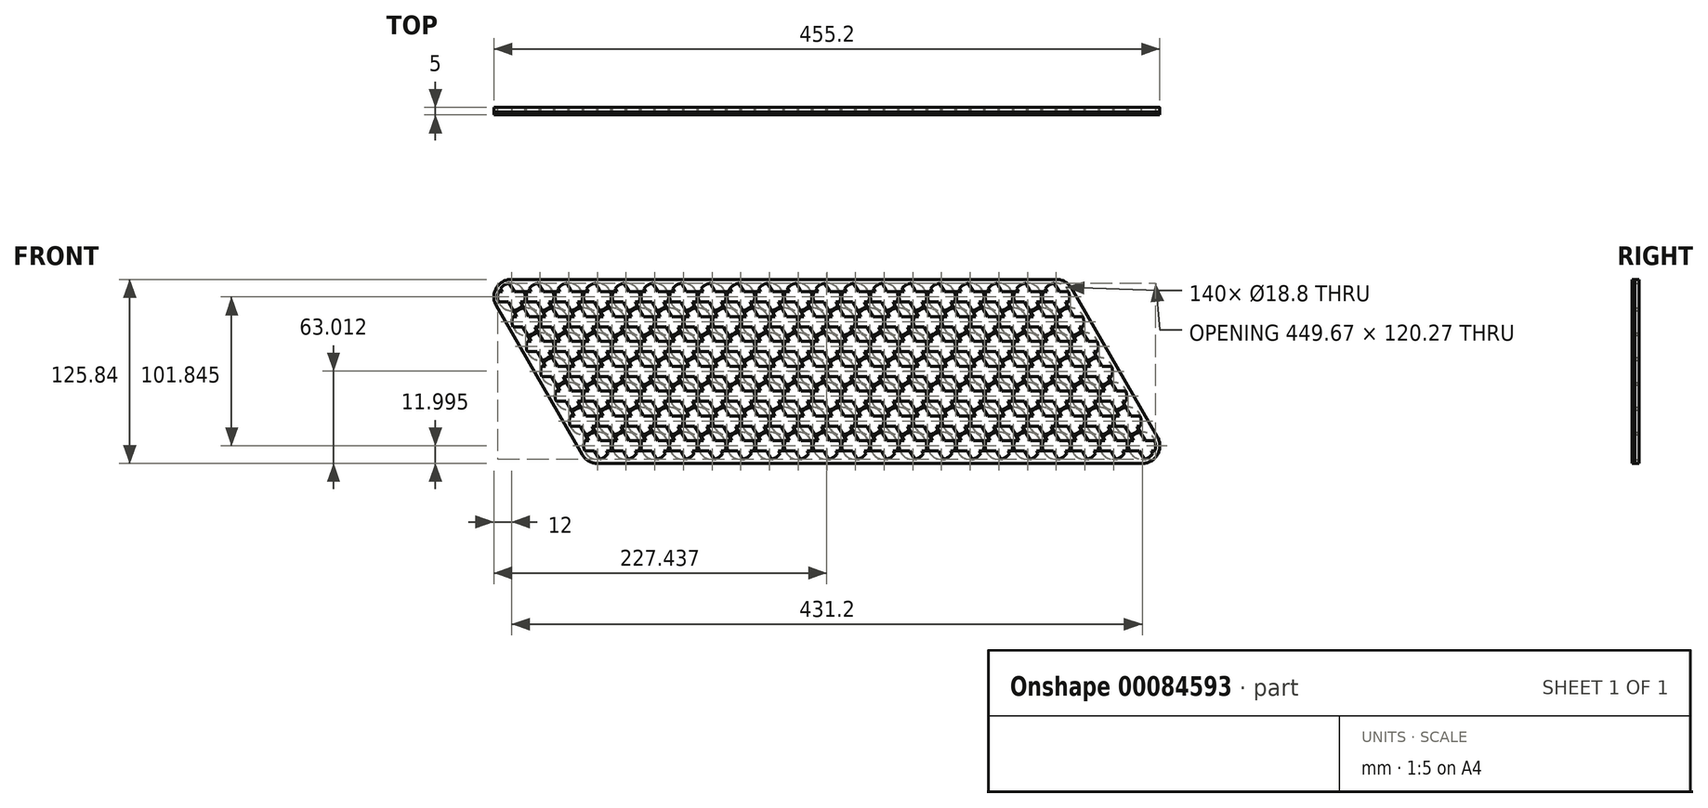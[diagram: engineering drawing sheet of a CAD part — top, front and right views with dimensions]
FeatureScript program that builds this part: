
annotation { "Feature Type Name" : "Feature", "Feature Type Description" : "" }
export const myFeature = defineFeature(function(context is Context, id is Id, definition is map)
    precondition{}
    {
        {
            var Q0;
            Q0=qCreatedBy(makeId("Front.planeOp"),FACE);
            var sketch = newSketch(context, id + "F0", { "sketchPlane" : qUnion([Q0]) });
            skLineSegment(sketch, "E0", {"start": v(0, 0) * mm, "end": v(79.44, 0) * mm, "construction": true});
            skLineSegment(sketch, "E1", {"start": v(0, 0) * mm, "end": v(43.4, -75.16) * mm, "construction": true});
            skCircle(sketch, "E2", {"center": v(0, 0) * mm, "radius": 9.4 * mm});
            skCircle(sketch, "E3.1.0.0", {"center": v(19.6, 0) * mm, "radius": 9.4 * mm});
            skCircle(sketch, "E3.2.0.0", {"center": v(39.2, 0) * mm, "radius": 9.4 * mm});
            skCircle(sketch, "E3.3.0.0", {"center": v(58.8, 0) * mm, "radius": 9.4 * mm});
            skCircle(sketch, "E3.4.0.0", {"center": v(78.4, 0) * mm, "radius": 9.4 * mm});
            skCircle(sketch, "E3.5.0.0", {"center": v(98, 0) * mm, "radius": 9.4 * mm});
            skCircle(sketch, "E3.6.0.0", {"center": v(117.6, 0) * mm, "radius": 9.4 * mm});
            skCircle(sketch, "E3.7.0.0", {"center": v(137.2, 0) * mm, "radius": 9.4 * mm});
            skCircle(sketch, "E3.8.0.0", {"center": v(156.8, 0) * mm, "radius": 9.4 * mm});
            skCircle(sketch, "E3.9.0.0", {"center": v(176.4, 0) * mm, "radius": 9.4 * mm});
            skCircle(sketch, "E3.10.0.0", {"center": v(196, 0) * mm, "radius": 9.4 * mm});
            skCircle(sketch, "E3.11.0.0", {"center": v(215.6, 0) * mm, "radius": 9.4 * mm});
            skCircle(sketch, "E3.12.0.0", {"center": v(235.2, 0) * mm, "radius": 9.4 * mm});
            skCircle(sketch, "E3.13.0.0", {"center": v(254.8, 0) * mm, "radius": 9.4 * mm});
            skCircle(sketch, "E3.14.0.0", {"center": v(274.4, 0) * mm, "radius": 9.4 * mm});
            skCircle(sketch, "E3.15.0.0", {"center": v(294, 0) * mm, "radius": 9.4 * mm});
            skCircle(sketch, "E3.16.0.0", {"center": v(313.6, 0) * mm, "radius": 9.4 * mm});
            skCircle(sketch, "E3.17.0.0", {"center": v(333.2, 0) * mm, "radius": 9.4 * mm});
            skCircle(sketch, "E3.18.0.0", {"center": v(352.8, 0) * mm, "radius": 9.4 * mm});
            skCircle(sketch, "E3.19.0.0", {"center": v(372.4, 0) * mm, "radius": 9.4 * mm});
            skLineSegment(sketch, "E3.direction1", {"start": v(0, 0) * mm, "end": v(19.6, 0) * mm, "construction": true});
            skCircle(sketch, "E4.1.0.0", {"center": v(9.8, -16.97) * mm, "radius": 9.4 * mm});
            skCircle(sketch, "E4.2.0.0", {"center": v(19.6, -33.95) * mm, "radius": 9.4 * mm});
            skCircle(sketch, "E4.3.0.0", {"center": v(29.4, -50.92) * mm, "radius": 9.4 * mm});
            skCircle(sketch, "E4.4.0.0", {"center": v(39.2, -67.9) * mm, "radius": 9.4 * mm});
            skCircle(sketch, "E4.5.0.0", {"center": v(49, -84.87) * mm, "radius": 9.4 * mm});
            skCircle(sketch, "E4.6.0.0", {"center": v(58.8, -101.84) * mm, "radius": 9.4 * mm});
            skLineSegment(sketch, "E4.direction1", {"start": v(0, 0) * mm, "end": v(9.8, -16.97) * mm, "construction": true});
            skCircle(sketch, "E5.1.0.0", {"center": v(29.4, -16.97) * mm, "radius": 9.4 * mm});
            skCircle(sketch, "E5.1.0.1", {"center": v(39.2, -33.95) * mm, "radius": 9.4 * mm});
            skCircle(sketch, "E5.1.0.2", {"center": v(49, -50.92) * mm, "radius": 9.4 * mm});
            skCircle(sketch, "E5.1.0.3", {"center": v(58.8, -67.9) * mm, "radius": 9.4 * mm});
            skCircle(sketch, "E5.1.0.4", {"center": v(68.6, -84.87) * mm, "radius": 9.4 * mm});
            skCircle(sketch, "E5.1.0.5", {"center": v(78.4, -101.84) * mm, "radius": 9.4 * mm});
            skCircle(sketch, "E5.2.0.0", {"center": v(49, -16.97) * mm, "radius": 9.4 * mm});
            skCircle(sketch, "E5.2.0.1", {"center": v(58.8, -33.95) * mm, "radius": 9.4 * mm});
            skCircle(sketch, "E5.2.0.2", {"center": v(68.6, -50.92) * mm, "radius": 9.4 * mm});
            skCircle(sketch, "E5.2.0.3", {"center": v(78.4, -67.9) * mm, "radius": 9.4 * mm});
            skCircle(sketch, "E5.2.0.4", {"center": v(88.2, -84.87) * mm, "radius": 9.4 * mm});
            skCircle(sketch, "E5.2.0.5", {"center": v(98, -101.84) * mm, "radius": 9.4 * mm});
            skCircle(sketch, "E5.3.0.0", {"center": v(68.6, -16.97) * mm, "radius": 9.4 * mm});
            skCircle(sketch, "E5.3.0.1", {"center": v(78.4, -33.95) * mm, "radius": 9.4 * mm});
            skCircle(sketch, "E5.3.0.2", {"center": v(88.2, -50.92) * mm, "radius": 9.4 * mm});
            skCircle(sketch, "E5.3.0.3", {"center": v(98, -67.9) * mm, "radius": 9.4 * mm});
            skCircle(sketch, "E5.3.0.4", {"center": v(107.8, -84.87) * mm, "radius": 9.4 * mm});
            skCircle(sketch, "E5.3.0.5", {"center": v(117.6, -101.84) * mm, "radius": 9.4 * mm});
            skCircle(sketch, "E5.4.0.0", {"center": v(88.2, -16.97) * mm, "radius": 9.4 * mm});
            skCircle(sketch, "E5.4.0.1", {"center": v(98, -33.95) * mm, "radius": 9.4 * mm});
            skCircle(sketch, "E5.4.0.2", {"center": v(107.8, -50.92) * mm, "radius": 9.4 * mm});
            skCircle(sketch, "E5.4.0.3", {"center": v(117.6, -67.9) * mm, "radius": 9.4 * mm});
            skCircle(sketch, "E5.4.0.4", {"center": v(127.4, -84.87) * mm, "radius": 9.4 * mm});
            skCircle(sketch, "E5.4.0.5", {"center": v(137.2, -101.84) * mm, "radius": 9.4 * mm});
            skCircle(sketch, "E5.5.0.0", {"center": v(107.8, -16.97) * mm, "radius": 9.4 * mm});
            skCircle(sketch, "E5.5.0.1", {"center": v(117.6, -33.95) * mm, "radius": 9.4 * mm});
            skCircle(sketch, "E5.5.0.2", {"center": v(127.4, -50.92) * mm, "radius": 9.4 * mm});
            skCircle(sketch, "E5.5.0.3", {"center": v(137.2, -67.9) * mm, "radius": 9.4 * mm});
            skCircle(sketch, "E5.5.0.4", {"center": v(147, -84.87) * mm, "radius": 9.4 * mm});
            skCircle(sketch, "E5.5.0.5", {"center": v(156.8, -101.84) * mm, "radius": 9.4 * mm});
            skCircle(sketch, "E5.6.0.0", {"center": v(127.4, -16.97) * mm, "radius": 9.4 * mm});
            skCircle(sketch, "E5.6.0.1", {"center": v(137.2, -33.95) * mm, "radius": 9.4 * mm});
            skCircle(sketch, "E5.6.0.2", {"center": v(147, -50.92) * mm, "radius": 9.4 * mm});
            skCircle(sketch, "E5.6.0.3", {"center": v(156.8, -67.9) * mm, "radius": 9.4 * mm});
            skCircle(sketch, "E5.6.0.4", {"center": v(166.6, -84.87) * mm, "radius": 9.4 * mm});
            skCircle(sketch, "E5.6.0.5", {"center": v(176.4, -101.84) * mm, "radius": 9.4 * mm});
            skCircle(sketch, "E5.7.0.0", {"center": v(147, -16.97) * mm, "radius": 9.4 * mm});
            skCircle(sketch, "E5.7.0.1", {"center": v(156.8, -33.95) * mm, "radius": 9.4 * mm});
            skCircle(sketch, "E5.7.0.2", {"center": v(166.6, -50.92) * mm, "radius": 9.4 * mm});
            skCircle(sketch, "E5.7.0.3", {"center": v(176.4, -67.9) * mm, "radius": 9.4 * mm});
            skCircle(sketch, "E5.7.0.4", {"center": v(186.2, -84.87) * mm, "radius": 9.4 * mm});
            skCircle(sketch, "E5.7.0.5", {"center": v(196, -101.84) * mm, "radius": 9.4 * mm});
            skCircle(sketch, "E5.8.0.0", {"center": v(166.6, -16.97) * mm, "radius": 9.4 * mm});
            skCircle(sketch, "E5.8.0.1", {"center": v(176.4, -33.95) * mm, "radius": 9.4 * mm});
            skCircle(sketch, "E5.8.0.2", {"center": v(186.2, -50.92) * mm, "radius": 9.4 * mm});
            skCircle(sketch, "E5.8.0.3", {"center": v(196, -67.9) * mm, "radius": 9.4 * mm});
            skCircle(sketch, "E5.8.0.4", {"center": v(205.8, -84.87) * mm, "radius": 9.4 * mm});
            skCircle(sketch, "E5.8.0.5", {"center": v(215.6, -101.84) * mm, "radius": 9.4 * mm});
            skCircle(sketch, "E5.9.0.0", {"center": v(186.2, -16.97) * mm, "radius": 9.4 * mm});
            skCircle(sketch, "E5.9.0.1", {"center": v(196, -33.95) * mm, "radius": 9.4 * mm});
            skCircle(sketch, "E5.9.0.2", {"center": v(205.8, -50.92) * mm, "radius": 9.4 * mm});
            skCircle(sketch, "E5.9.0.3", {"center": v(215.6, -67.9) * mm, "radius": 9.4 * mm});
            skCircle(sketch, "E5.9.0.4", {"center": v(225.4, -84.87) * mm, "radius": 9.4 * mm});
            skCircle(sketch, "E5.9.0.5", {"center": v(235.2, -101.84) * mm, "radius": 9.4 * mm});
            skCircle(sketch, "E5.10.0.0", {"center": v(205.8, -16.97) * mm, "radius": 9.4 * mm});
            skCircle(sketch, "E5.10.0.1", {"center": v(215.6, -33.95) * mm, "radius": 9.4 * mm});
            skCircle(sketch, "E5.10.0.2", {"center": v(225.4, -50.92) * mm, "radius": 9.4 * mm});
            skCircle(sketch, "E5.10.0.3", {"center": v(235.2, -67.9) * mm, "radius": 9.4 * mm});
            skCircle(sketch, "E5.10.0.4", {"center": v(245, -84.87) * mm, "radius": 9.4 * mm});
            skCircle(sketch, "E5.10.0.5", {"center": v(254.8, -101.84) * mm, "radius": 9.4 * mm});
            skCircle(sketch, "E5.11.0.0", {"center": v(225.4, -16.97) * mm, "radius": 9.4 * mm});
            skCircle(sketch, "E5.11.0.1", {"center": v(235.2, -33.95) * mm, "radius": 9.4 * mm});
            skCircle(sketch, "E5.11.0.2", {"center": v(245, -50.92) * mm, "radius": 9.4 * mm});
            skCircle(sketch, "E5.11.0.3", {"center": v(254.8, -67.9) * mm, "radius": 9.4 * mm});
            skCircle(sketch, "E5.11.0.4", {"center": v(264.6, -84.87) * mm, "radius": 9.4 * mm});
            skCircle(sketch, "E5.11.0.5", {"center": v(274.4, -101.84) * mm, "radius": 9.4 * mm});
            skCircle(sketch, "E5.12.0.0", {"center": v(245, -16.97) * mm, "radius": 9.4 * mm});
            skCircle(sketch, "E5.12.0.1", {"center": v(254.8, -33.95) * mm, "radius": 9.4 * mm});
            skCircle(sketch, "E5.12.0.2", {"center": v(264.6, -50.92) * mm, "radius": 9.4 * mm});
            skCircle(sketch, "E5.12.0.3", {"center": v(274.4, -67.9) * mm, "radius": 9.4 * mm});
            skCircle(sketch, "E5.12.0.4", {"center": v(284.2, -84.87) * mm, "radius": 9.4 * mm});
            skCircle(sketch, "E5.12.0.5", {"center": v(294, -101.84) * mm, "radius": 9.4 * mm});
            skCircle(sketch, "E5.13.0.0", {"center": v(264.6, -16.97) * mm, "radius": 9.4 * mm});
            skCircle(sketch, "E5.13.0.1", {"center": v(274.4, -33.95) * mm, "radius": 9.4 * mm});
            skCircle(sketch, "E5.13.0.2", {"center": v(284.2, -50.92) * mm, "radius": 9.4 * mm});
            skCircle(sketch, "E5.13.0.3", {"center": v(294, -67.9) * mm, "radius": 9.4 * mm});
            skCircle(sketch, "E5.13.0.4", {"center": v(303.8, -84.87) * mm, "radius": 9.4 * mm});
            skCircle(sketch, "E5.13.0.5", {"center": v(313.6, -101.84) * mm, "radius": 9.4 * mm});
            skCircle(sketch, "E5.14.0.0", {"center": v(284.2, -16.97) * mm, "radius": 9.4 * mm});
            skCircle(sketch, "E5.14.0.1", {"center": v(294, -33.95) * mm, "radius": 9.4 * mm});
            skCircle(sketch, "E5.14.0.2", {"center": v(303.8, -50.92) * mm, "radius": 9.4 * mm});
            skCircle(sketch, "E5.14.0.3", {"center": v(313.6, -67.9) * mm, "radius": 9.4 * mm});
            skCircle(sketch, "E5.14.0.4", {"center": v(323.4, -84.87) * mm, "radius": 9.4 * mm});
            skCircle(sketch, "E5.14.0.5", {"center": v(333.2, -101.84) * mm, "radius": 9.4 * mm});
            skCircle(sketch, "E5.15.0.0", {"center": v(303.8, -16.97) * mm, "radius": 9.4 * mm});
            skCircle(sketch, "E5.15.0.1", {"center": v(313.6, -33.95) * mm, "radius": 9.4 * mm});
            skCircle(sketch, "E5.15.0.2", {"center": v(323.4, -50.92) * mm, "radius": 9.4 * mm});
            skCircle(sketch, "E5.15.0.3", {"center": v(333.2, -67.9) * mm, "radius": 9.4 * mm});
            skCircle(sketch, "E5.15.0.4", {"center": v(343, -84.87) * mm, "radius": 9.4 * mm});
            skCircle(sketch, "E5.15.0.5", {"center": v(352.8, -101.84) * mm, "radius": 9.4 * mm});
            skCircle(sketch, "E5.16.0.0", {"center": v(323.4, -16.97) * mm, "radius": 9.4 * mm});
            skCircle(sketch, "E5.16.0.1", {"center": v(333.2, -33.95) * mm, "radius": 9.4 * mm});
            skCircle(sketch, "E5.16.0.2", {"center": v(343, -50.92) * mm, "radius": 9.4 * mm});
            skCircle(sketch, "E5.16.0.3", {"center": v(352.8, -67.9) * mm, "radius": 9.4 * mm});
            skCircle(sketch, "E5.16.0.4", {"center": v(362.6, -84.87) * mm, "radius": 9.4 * mm});
            skCircle(sketch, "E5.16.0.5", {"center": v(372.4, -101.84) * mm, "radius": 9.4 * mm});
            skCircle(sketch, "E5.17.0.0", {"center": v(343, -16.97) * mm, "radius": 9.4 * mm});
            skCircle(sketch, "E5.17.0.1", {"center": v(352.8, -33.95) * mm, "radius": 9.4 * mm});
            skCircle(sketch, "E5.17.0.2", {"center": v(362.6, -50.92) * mm, "radius": 9.4 * mm});
            skCircle(sketch, "E5.17.0.3", {"center": v(372.4, -67.9) * mm, "radius": 9.4 * mm});
            skCircle(sketch, "E5.17.0.4", {"center": v(382.2, -84.87) * mm, "radius": 9.4 * mm});
            skCircle(sketch, "E5.17.0.5", {"center": v(392, -101.84) * mm, "radius": 9.4 * mm});
            skCircle(sketch, "E5.18.0.0", {"center": v(362.6, -16.97) * mm, "radius": 9.4 * mm});
            skCircle(sketch, "E5.18.0.1", {"center": v(372.4, -33.95) * mm, "radius": 9.4 * mm});
            skCircle(sketch, "E5.18.0.2", {"center": v(382.2, -50.92) * mm, "radius": 9.4 * mm});
            skCircle(sketch, "E5.18.0.3", {"center": v(392, -67.9) * mm, "radius": 9.4 * mm});
            skCircle(sketch, "E5.18.0.4", {"center": v(401.8, -84.87) * mm, "radius": 9.4 * mm});
            skCircle(sketch, "E5.18.0.5", {"center": v(411.6, -101.84) * mm, "radius": 9.4 * mm});
            skCircle(sketch, "E5.19.0.0", {"center": v(382.2, -16.97) * mm, "radius": 9.4 * mm});
            skCircle(sketch, "E5.19.0.1", {"center": v(392, -33.95) * mm, "radius": 9.4 * mm});
            skCircle(sketch, "E5.19.0.2", {"center": v(401.8, -50.92) * mm, "radius": 9.4 * mm});
            skCircle(sketch, "E5.19.0.3", {"center": v(411.6, -67.9) * mm, "radius": 9.4 * mm});
            skCircle(sketch, "E5.19.0.4", {"center": v(421.4, -84.87) * mm, "radius": 9.4 * mm});
            skCircle(sketch, "E5.19.0.5", {"center": v(431.2, -101.84) * mm, "radius": 9.4 * mm});
            skLineSegment(sketch, "E5.direction1", {"start": v(9.8, -16.97) * mm, "end": v(29.4, -16.97) * mm, "construction": true});
            skLineSegment(sketch, "E6", {"start": v(0, 0) * mm, "end": v(372.4, 0) * mm, "construction": true});
            skLineSegment(sketch, "E7", {"start": v(372.4, 0) * mm, "end": v(441, -118.82) * mm, "construction": true});
            skLineSegment(sketch, "E8", {"start": v(441, -118.82) * mm, "end": v(68.6, -118.82) * mm, "construction": true});
            skLineSegment(sketch, "E9", {"start": v(68.6, -118.82) * mm, "end": v(0, 0) * mm, "construction": true});
            skArc(sketch, "E10", {"start": v(48.4, -107.84) * mm, "mid": v(52.8, -112.24) * mm, "end": v(58.8, -113.84) * mm});
            skArc(sketch, "E11", {"start": v(431.2, -113.84) * mm, "mid": v(441.6, -107.84) * mm, "end": v(441.6, -95.84) * mm});
            skArc(sketch, "E12", {"start": v(382.8, 6) * mm, "mid": v(378.4, 10.4) * mm, "end": v(372.4, 12) * mm});
            skArc(sketch, "E13", {"start": v(0, 12) * mm, "mid": v(-10.4, 6) * mm, "end": v(-10.4, -6) * mm});
            skLineSegment(sketch, "E14", {"start": v(0, 12) * mm, "end": v(372.4, 12) * mm});
            skLineSegment(sketch, "E15", {"start": v(-10.4, -6) * mm, "end": v(48.4, -107.84) * mm});
            skLineSegment(sketch, "E16", {"start": v(58.8, -113.84) * mm, "end": v(431.2, -113.84) * mm});
            skLineSegment(sketch, "E17", {"start": v(441.6, -95.84) * mm, "end": v(382.8, 6) * mm});
            skLineSegment(sketch, "E18", {"start": v(441.6, -107.84) * mm, "end": v(500.4, -6) * mm, "construction": true});
            skLineSegment(sketch, "E19", {"start": v(372.4, 12) * mm, "end": v(490, 12) * mm, "construction": true});
            skPoint(sketch, "E20.visualSharp", {"position": v(510.78, 12) * mm});
            skArc(sketch, "E20.filletArc", {"start": v(500.4, -6) * mm, "mid": v(500.4, 6) * mm, "end": v(490, 12) * mm, "construction": true});
            skSolve(sketch);
        }
        {
            var Q0;
            Q0=makeQuery(id+"F0.imprint","IMPRINT",FACE,{"disambiguationData":[TD([[makeQuery(id+"F0.imprint","IMPRINT",EDGE,{"derivedFrom":sQuery(id+"F0.wireOp",EDGE,"E2")}),-1.0]])]});
            extrude(context, id + "F1", {"entities" : qUnion([Q0]), "depth" : 3 * mm});
        }
        {
            var Q0;
            Q0=makeQuery(id+"F1.opExtrude","CAP_FACE",FACE,{"disambiguationData":[OSD([sQuery(id+"F0.wireOp",EDGE,"E2"),sQuery(id+"F0.wireOp",EDGE,"E3.1.0.0"),sQuery(id+"F0.wireOp",EDGE,"E3.2.0.0"),sQuery(id+"F0.wireOp",EDGE,"E3.3.0.0"),sQuery(id+"F0.wireOp",EDGE,"E3.4.0.0"),sQuery(id+"F0.wireOp",EDGE,"E3.5.0.0"),sQuery(id+"F0.wireOp",EDGE,"E3.6.0.0"),sQuery(id+"F0.wireOp",EDGE,"E3.7.0.0"),sQuery(id+"F0.wireOp",EDGE,"E3.8.0.0"),sQuery(id+"F0.wireOp",EDGE,"E3.9.0.0"),sQuery(id+"F0.wireOp",EDGE,"E3.10.0.0"),sQuery(id+"F0.wireOp",EDGE,"E3.11.0.0"),sQuery(id+"F0.wireOp",EDGE,"E3.12.0.0"),sQuery(id+"F0.wireOp",EDGE,"E3.13.0.0"),sQuery(id+"F0.wireOp",EDGE,"E3.14.0.0"),sQuery(id+"F0.wireOp",EDGE,"E3.15.0.0"),sQuery(id+"F0.wireOp",EDGE,"E3.16.0.0"),sQuery(id+"F0.wireOp",EDGE,"E3.17.0.0"),sQuery(id+"F0.wireOp",EDGE,"E3.18.0.0"),sQuery(id+"F0.wireOp",EDGE,"E3.19.0.0"),sQuery(id+"F0.wireOp",EDGE,"E4.1.0.0"),sQuery(id+"F0.wireOp",EDGE,"E4.2.0.0"),sQuery(id+"F0.wireOp",EDGE,"E4.3.0.0"),sQuery(id+"F0.wireOp",EDGE,"E4.4.0.0"),sQuery(id+"F0.wireOp",EDGE,"E4.5.0.0"),sQuery(id+"F0.wireOp",EDGE,"E4.6.0.0"),sQuery(id+"F0.wireOp",EDGE,"E5.1.0.0"),sQuery(id+"F0.wireOp",EDGE,"E5.1.0.1"),sQuery(id+"F0.wireOp",EDGE,"E5.1.0.2"),sQuery(id+"F0.wireOp",EDGE,"E5.1.0.3"),sQuery(id+"F0.wireOp",EDGE,"E5.1.0.4"),sQuery(id+"F0.wireOp",EDGE,"E5.1.0.5"),sQuery(id+"F0.wireOp",EDGE,"E5.2.0.0"),sQuery(id+"F0.wireOp",EDGE,"E5.2.0.1"),sQuery(id+"F0.wireOp",EDGE,"E5.2.0.2"),sQuery(id+"F0.wireOp",EDGE,"E5.2.0.3"),sQuery(id+"F0.wireOp",EDGE,"E5.2.0.4"),sQuery(id+"F0.wireOp",EDGE,"E5.2.0.5"),sQuery(id+"F0.wireOp",EDGE,"E5.3.0.0"),sQuery(id+"F0.wireOp",EDGE,"E5.3.0.1"),sQuery(id+"F0.wireOp",EDGE,"E5.3.0.2"),sQuery(id+"F0.wireOp",EDGE,"E5.3.0.3"),sQuery(id+"F0.wireOp",EDGE,"E5.3.0.4"),sQuery(id+"F0.wireOp",EDGE,"E5.3.0.5"),sQuery(id+"F0.wireOp",EDGE,"E5.4.0.0"),sQuery(id+"F0.wireOp",EDGE,"E5.4.0.1"),sQuery(id+"F0.wireOp",EDGE,"E5.4.0.2"),sQuery(id+"F0.wireOp",EDGE,"E5.4.0.3"),sQuery(id+"F0.wireOp",EDGE,"E5.4.0.4"),sQuery(id+"F0.wireOp",EDGE,"E5.4.0.5"),sQuery(id+"F0.wireOp",EDGE,"E5.5.0.0"),sQuery(id+"F0.wireOp",EDGE,"E5.5.0.1"),sQuery(id+"F0.wireOp",EDGE,"E5.5.0.2"),sQuery(id+"F0.wireOp",EDGE,"E5.5.0.3"),sQuery(id+"F0.wireOp",EDGE,"E5.5.0.4"),sQuery(id+"F0.wireOp",EDGE,"E5.5.0.5"),sQuery(id+"F0.wireOp",EDGE,"E5.6.0.0"),sQuery(id+"F0.wireOp",EDGE,"E5.6.0.1"),sQuery(id+"F0.wireOp",EDGE,"E5.6.0.2"),sQuery(id+"F0.wireOp",EDGE,"E5.6.0.3"),sQuery(id+"F0.wireOp",EDGE,"E5.6.0.4"),sQuery(id+"F0.wireOp",EDGE,"E5.6.0.5"),sQuery(id+"F0.wireOp",EDGE,"E5.7.0.0"),sQuery(id+"F0.wireOp",EDGE,"E5.7.0.1"),sQuery(id+"F0.wireOp",EDGE,"E5.7.0.2"),sQuery(id+"F0.wireOp",EDGE,"E5.7.0.3"),sQuery(id+"F0.wireOp",EDGE,"E5.7.0.4"),sQuery(id+"F0.wireOp",EDGE,"E5.7.0.5"),sQuery(id+"F0.wireOp",EDGE,"E5.8.0.0"),sQuery(id+"F0.wireOp",EDGE,"E5.8.0.1"),sQuery(id+"F0.wireOp",EDGE,"E5.8.0.2"),sQuery(id+"F0.wireOp",EDGE,"E5.8.0.3"),sQuery(id+"F0.wireOp",EDGE,"E5.8.0.4"),sQuery(id+"F0.wireOp",EDGE,"E5.8.0.5"),sQuery(id+"F0.wireOp",EDGE,"E5.9.0.0"),sQuery(id+"F0.wireOp",EDGE,"E5.9.0.1"),sQuery(id+"F0.wireOp",EDGE,"E5.9.0.2"),sQuery(id+"F0.wireOp",EDGE,"E5.9.0.3"),sQuery(id+"F0.wireOp",EDGE,"E5.9.0.4"),sQuery(id+"F0.wireOp",EDGE,"E5.9.0.5"),sQuery(id+"F0.wireOp",EDGE,"E5.10.0.0"),sQuery(id+"F0.wireOp",EDGE,"E5.10.0.1"),sQuery(id+"F0.wireOp",EDGE,"E5.10.0.2"),sQuery(id+"F0.wireOp",EDGE,"E5.10.0.3"),sQuery(id+"F0.wireOp",EDGE,"E5.10.0.4"),sQuery(id+"F0.wireOp",EDGE,"E5.10.0.5"),sQuery(id+"F0.wireOp",EDGE,"E5.11.0.0"),sQuery(id+"F0.wireOp",EDGE,"E5.11.0.1"),sQuery(id+"F0.wireOp",EDGE,"E5.11.0.2"),sQuery(id+"F0.wireOp",EDGE,"E5.11.0.3"),sQuery(id+"F0.wireOp",EDGE,"E5.11.0.4"),sQuery(id+"F0.wireOp",EDGE,"E5.11.0.5"),sQuery(id+"F0.wireOp",EDGE,"E5.12.0.0"),sQuery(id+"F0.wireOp",EDGE,"E5.12.0.1"),sQuery(id+"F0.wireOp",EDGE,"E5.12.0.2"),sQuery(id+"F0.wireOp",EDGE,"E5.12.0.3"),sQuery(id+"F0.wireOp",EDGE,"E5.12.0.4"),sQuery(id+"F0.wireOp",EDGE,"E5.12.0.5"),sQuery(id+"F0.wireOp",EDGE,"E5.13.0.0"),sQuery(id+"F0.wireOp",EDGE,"E5.13.0.1"),sQuery(id+"F0.wireOp",EDGE,"E5.13.0.2"),sQuery(id+"F0.wireOp",EDGE,"E5.13.0.3"),sQuery(id+"F0.wireOp",EDGE,"E5.13.0.4"),sQuery(id+"F0.wireOp",EDGE,"E5.13.0.5"),sQuery(id+"F0.wireOp",EDGE,"E5.14.0.0"),sQuery(id+"F0.wireOp",EDGE,"E5.14.0.1"),sQuery(id+"F0.wireOp",EDGE,"E5.14.0.2"),sQuery(id+"F0.wireOp",EDGE,"E5.14.0.3"),sQuery(id+"F0.wireOp",EDGE,"E5.14.0.4"),sQuery(id+"F0.wireOp",EDGE,"E5.14.0.5"),sQuery(id+"F0.wireOp",EDGE,"E5.15.0.0"),sQuery(id+"F0.wireOp",EDGE,"E5.15.0.1"),sQuery(id+"F0.wireOp",EDGE,"E5.15.0.2"),sQuery(id+"F0.wireOp",EDGE,"E5.15.0.3"),sQuery(id+"F0.wireOp",EDGE,"E5.15.0.4"),sQuery(id+"F0.wireOp",EDGE,"E5.15.0.5"),sQuery(id+"F0.wireOp",EDGE,"E5.16.0.0"),sQuery(id+"F0.wireOp",EDGE,"E5.16.0.1"),sQuery(id+"F0.wireOp",EDGE,"E5.16.0.2"),sQuery(id+"F0.wireOp",EDGE,"E5.16.0.3"),sQuery(id+"F0.wireOp",EDGE,"E5.16.0.4"),sQuery(id+"F0.wireOp",EDGE,"E5.16.0.5"),sQuery(id+"F0.wireOp",EDGE,"E5.17.0.0"),sQuery(id+"F0.wireOp",EDGE,"E5.17.0.1"),sQuery(id+"F0.wireOp",EDGE,"E5.17.0.2"),sQuery(id+"F0.wireOp",EDGE,"E5.17.0.3"),sQuery(id+"F0.wireOp",EDGE,"E5.17.0.4"),sQuery(id+"F0.wireOp",EDGE,"E5.17.0.5"),sQuery(id+"F0.wireOp",EDGE,"E5.18.0.0"),sQuery(id+"F0.wireOp",EDGE,"E5.18.0.1"),sQuery(id+"F0.wireOp",EDGE,"E5.18.0.2"),sQuery(id+"F0.wireOp",EDGE,"E5.18.0.3"),sQuery(id+"F0.wireOp",EDGE,"E5.18.0.4"),sQuery(id+"F0.wireOp",EDGE,"E5.18.0.5"),sQuery(id+"F0.wireOp",EDGE,"E5.19.0.0"),sQuery(id+"F0.wireOp",EDGE,"E5.19.0.1"),sQuery(id+"F0.wireOp",EDGE,"E5.19.0.2"),sQuery(id+"F0.wireOp",EDGE,"E5.19.0.3"),sQuery(id+"F0.wireOp",EDGE,"E5.19.0.4"),sQuery(id+"F0.wireOp",EDGE,"E5.19.0.5"),sQuery(id+"F0.wireOp",EDGE,"E10"),sQuery(id+"F0.wireOp",EDGE,"E11"),sQuery(id+"F0.wireOp",EDGE,"E12"),sQuery(id+"F0.wireOp",EDGE,"E13"),sQuery(id+"F0.wireOp",EDGE,"E14"),sQuery(id+"F0.wireOp",EDGE,"E15"),sQuery(id+"F0.wireOp",EDGE,"E16"),sQuery(id+"F0.wireOp",EDGE,"E17")])],"isStart":false});
            var sketch = newSketch(context, id + "F2", { "sketchPlane" : qUnion([Q0]) });
            skLineSegment(sketch, "E21.0", {"start": v(0, 12) * mm, "end": v(372.4, 12) * mm});
            skArc(sketch, "E21.1", {"start": v(0, 12) * mm, "mid": v(-10.4, 6) * mm, "end": v(-10.4, -6) * mm});
            skLineSegment(sketch, "E21.2", {"start": v(-10.4, -6) * mm, "end": v(48.4, -107.84) * mm});
            skArc(sketch, "E21.3", {"start": v(382.8, 6) * mm, "mid": v(378.4, 10.4) * mm, "end": v(372.4, 12) * mm});
            skLineSegment(sketch, "E21.4", {"start": v(441.6, -95.84) * mm, "end": v(382.8, 6) * mm});
            skArc(sketch, "E21.5", {"start": v(431.2, -113.84) * mm, "mid": v(441.6, -107.84) * mm, "end": v(441.6, -95.84) * mm});
            skLineSegment(sketch, "E21.6", {"start": v(58.8, -113.84) * mm, "end": v(431.2, -113.84) * mm});
            skArc(sketch, "E21.7", {"start": v(48.4, -107.84) * mm, "mid": v(52.8, -112.24) * mm, "end": v(58.8, -113.84) * mm});
            skSolve(sketch);
        }
        {
            var Q0;
            Q0 = qSketchRegion(id + "F2", true);
            extrude(context, id + "F3", {"entities" : qUnion([Q0]), "depth" : 2 * mm});
        }
        {
            var Q0;
            Q0=makeQuery(id+"F3.opExtrude","CAP_FACE",FACE,{"disambiguationData":[OSD([sQuery(id+"F2.wireOp",EDGE,"E21.0"),sQuery(id+"F2.wireOp",EDGE,"E21.1"),sQuery(id+"F2.wireOp",EDGE,"E21.2"),sQuery(id+"F2.wireOp",EDGE,"E21.3"),sQuery(id+"F2.wireOp",EDGE,"E21.4"),sQuery(id+"F2.wireOp",EDGE,"E21.5"),sQuery(id+"F2.wireOp",EDGE,"E21.6"),sQuery(id+"F2.wireOp",EDGE,"E21.7")])],"isStart":false});
            var sketch = newSketch(context, id + "F4", { "sketchPlane" : qUnion([Q0]) });
            skLineSegment(sketch, "E22", {"start": v(0, 0) * mm, "end": v(58.8, -101.84) * mm, "construction": true});
            skLineSegment(sketch, "E23", {"start": v(58.8, -101.84) * mm, "end": v(431.2, -101.84) * mm, "construction": true});
            skLineSegment(sketch, "E24", {"start": v(431.2, -101.84) * mm, "end": v(372.4, 0) * mm, "construction": true});
            skLineSegment(sketch, "E25", {"start": v(372.4, 0) * mm, "end": v(0, 0) * mm, "construction": true});
            skLineSegment(sketch, "E26", {"start": v(-8.72, 3.5) * mm, "end": v(380.69, 3.5) * mm});
            skLineSegment(sketch, "E27.MirrorCS", {"start": v(-8.72, -3.5) * mm, "end": v(380.9, -3.5) * mm});
            skArc(sketch, "E28.0", {"start": v(-8.72, 3.5) * mm, "mid": v(-9.4, 0) * mm, "end": v(-8.72, -3.5) * mm});
            skArc(sketch, "E29.trimOffspring", {"start": v(380.9, -3.5) * mm, "mid": v(381.47, 0.02) * mm, "end": v(380.69, 3.5) * mm});
            skPoint(sketch, "E30.orphan", {"position": v(456.43, 3.5) * mm});
            skPoint(sketch, "E31.orphan", {"position": v(456.43, -3.5) * mm});
            skPoint(sketch, "E32.orphan", {"position": v(-45.25, 3.5) * mm});
            skPoint(sketch, "E33.orphan", {"position": v(-45.25, -3.5) * mm});
            skLineSegment(sketch, "E34.0.1.0", {"start": v(1.08, -13.47) * mm, "end": v(390.49, -13.47) * mm});
            skLineSegment(sketch, "E34.0.1.1", {"start": v(1.08, -20.47) * mm, "end": v(390.7, -20.47) * mm});
            skArc(sketch, "E34.0.1.2", {"start": v(1.08, -13.47) * mm, "mid": v(0.4, -16.97) * mm, "end": v(1.08, -20.47) * mm});
            skArc(sketch, "E34.0.1.3", {"start": v(390.7, -20.47) * mm, "mid": v(391.27, -16.95) * mm, "end": v(390.49, -13.47) * mm});
            skLineSegment(sketch, "E34.0.2.0", {"start": v(10.88, -30.45) * mm, "end": v(400.29, -30.45) * mm});
            skLineSegment(sketch, "E34.0.2.1", {"start": v(10.88, -37.45) * mm, "end": v(400.5, -37.45) * mm});
            skArc(sketch, "E34.0.2.2", {"start": v(10.88, -30.45) * mm, "mid": v(10.2, -33.95) * mm, "end": v(10.88, -37.45) * mm});
            skArc(sketch, "E34.0.2.3", {"start": v(400.5, -37.45) * mm, "mid": v(401.07, -33.93) * mm, "end": v(400.29, -30.45) * mm});
            skLineSegment(sketch, "E34.0.3.0", {"start": v(20.68, -47.42) * mm, "end": v(410.09, -47.42) * mm});
            skLineSegment(sketch, "E34.0.3.1", {"start": v(20.68, -54.42) * mm, "end": v(410.3, -54.42) * mm});
            skArc(sketch, "E34.0.3.2", {"start": v(20.68, -47.42) * mm, "mid": v(20, -50.92) * mm, "end": v(20.68, -54.42) * mm});
            skArc(sketch, "E34.0.3.3", {"start": v(410.3, -54.42) * mm, "mid": v(410.87, -50.9) * mm, "end": v(410.09, -47.42) * mm});
            skLineSegment(sketch, "E34.0.4.0", {"start": v(30.48, -64.4) * mm, "end": v(419.89, -64.4) * mm});
            skLineSegment(sketch, "E34.0.4.1", {"start": v(30.48, -71.4) * mm, "end": v(420.1, -71.4) * mm});
            skArc(sketch, "E34.0.4.2", {"start": v(30.48, -64.4) * mm, "mid": v(29.8, -67.9) * mm, "end": v(30.48, -71.4) * mm});
            skArc(sketch, "E34.0.4.3", {"start": v(420.1, -71.4) * mm, "mid": v(420.67, -67.88) * mm, "end": v(419.89, -64.4) * mm});
            skLineSegment(sketch, "E34.0.5.0", {"start": v(40.28, -81.37) * mm, "end": v(429.69, -81.37) * mm});
            skLineSegment(sketch, "E34.0.5.1", {"start": v(40.28, -88.37) * mm, "end": v(429.9, -88.37) * mm});
            skArc(sketch, "E34.0.5.2", {"start": v(40.28, -81.37) * mm, "mid": v(39.6, -84.87) * mm, "end": v(40.28, -88.37) * mm});
            skArc(sketch, "E34.0.5.3", {"start": v(429.9, -88.37) * mm, "mid": v(430.47, -84.85) * mm, "end": v(429.69, -81.37) * mm});
            skLineSegment(sketch, "E34.0.6.0", {"start": v(50.08, -98.34) * mm, "end": v(439.49, -98.34) * mm});
            skLineSegment(sketch, "E34.0.6.1", {"start": v(50.08, -105.34) * mm, "end": v(439.7, -105.34) * mm});
            skArc(sketch, "E34.0.6.2", {"start": v(50.08, -98.34) * mm, "mid": v(49.4, -101.84) * mm, "end": v(50.08, -105.34) * mm});
            skArc(sketch, "E34.0.6.3", {"start": v(439.7, -105.34) * mm, "mid": v(440.27, -101.82) * mm, "end": v(439.49, -98.34) * mm});
            skLineSegment(sketch, "E34.direction1", {"start": v(-8.72, 3.5) * mm, "end": v(16.28, 3.5) * mm, "construction": true});
            skLineSegment(sketch, "E34.direction2", {"start": v(-8.72, 3.5) * mm, "end": v(1.08, -13.47) * mm, "construction": true});
            skSolve(sketch);
        }
        {
            var Q0;
            Q0 = qSketchRegion(id + "F4", true);
            extrude(context, id + "F5", {"entities" : qUnion([Q0]), "operationType" : NewBodyOperationType.REMOVE, "endBound" : BoundingType.UP_TO_NEXT, "oppositeDirection" : true, "depth" : 25 * mm});
        }
        {
            var Q0;
            Q0=makeQuery(id+"F3.opExtrude","CAP_FACE",FACE,{"disambiguationData":[OSD([sQuery(id+"F2.wireOp",EDGE,"E21.0"),sQuery(id+"F2.wireOp",EDGE,"E21.1"),sQuery(id+"F2.wireOp",EDGE,"E21.2"),sQuery(id+"F2.wireOp",EDGE,"E21.3"),sQuery(id+"F2.wireOp",EDGE,"E21.4"),sQuery(id+"F2.wireOp",EDGE,"E21.5"),sQuery(id+"F2.wireOp",EDGE,"E21.6"),sQuery(id+"F2.wireOp",EDGE,"E21.7")])],"isStart":false});
            var sketch = newSketch(context, id + "F6", { "sketchPlane" : qUnion([Q0]) });
            skLineSegment(sketch, "E35", {"start": v(0, 0) * mm, "end": v(58.8, -101.84) * mm, "construction": true});
            skLineSegment(sketch, "E36", {"start": v(-1.33, 9.3) * mm, "end": v(65.94, -107.21) * mm});
            skLineSegment(sketch, "E37.MirrorCS", {"start": v(-7.4, 5.8) * mm, "end": v(60.02, -110.96) * mm});
            skArc(sketch, "E38.0", {"start": v(-1.33, 9.3) * mm, "mid": v(-4.7, 8.14) * mm, "end": v(-7.4, 5.8) * mm});
            skArc(sketch, "E39.trimOffspring", {"start": v(60.02, -110.96) * mm, "mid": v(63.34, -109.66) * mm, "end": v(65.94, -107.21) * mm});
            skPoint(sketch, "E40.orphan", {"position": v(72.39, -132.38) * mm});
            skPoint(sketch, "E41.orphan", {"position": v(78.45, -128.88) * mm});
            skPoint(sketch, "E42.orphan", {"position": v(-7.3, 19.64) * mm});
            skPoint(sketch, "E43.orphan", {"position": v(-13.36, 16.14) * mm});
            skArc(sketch, "E44.1.0.0", {"start": v(18.27, 9.3) * mm, "mid": v(14.9, 8.14) * mm, "end": v(12.2, 5.8) * mm});
            skLineSegment(sketch, "E44.1.0.1", {"start": v(12.2, 5.8) * mm, "end": v(79.62, -110.96) * mm});
            skLineSegment(sketch, "E44.1.0.2", {"start": v(18.27, 9.3) * mm, "end": v(85.54, -107.21) * mm});
            skArc(sketch, "E44.1.0.3", {"start": v(79.62, -110.96) * mm, "mid": v(82.94, -109.66) * mm, "end": v(85.54, -107.21) * mm});
            skArc(sketch, "E44.2.0.0", {"start": v(37.87, 9.3) * mm, "mid": v(34.5, 8.14) * mm, "end": v(31.8, 5.8) * mm});
            skLineSegment(sketch, "E44.2.0.1", {"start": v(31.8, 5.8) * mm, "end": v(99.22, -110.96) * mm});
            skLineSegment(sketch, "E44.2.0.2", {"start": v(37.87, 9.3) * mm, "end": v(105.14, -107.21) * mm});
            skArc(sketch, "E44.2.0.3", {"start": v(99.22, -110.96) * mm, "mid": v(102.54, -109.66) * mm, "end": v(105.14, -107.21) * mm});
            skArc(sketch, "E44.3.0.0", {"start": v(57.47, 9.3) * mm, "mid": v(54.1, 8.14) * mm, "end": v(51.4, 5.8) * mm});
            skLineSegment(sketch, "E44.3.0.1", {"start": v(51.4, 5.8) * mm, "end": v(118.82, -110.96) * mm});
            skLineSegment(sketch, "E44.3.0.2", {"start": v(57.47, 9.3) * mm, "end": v(124.74, -107.21) * mm});
            skArc(sketch, "E44.3.0.3", {"start": v(118.82, -110.96) * mm, "mid": v(122.14, -109.66) * mm, "end": v(124.74, -107.21) * mm});
            skArc(sketch, "E44.4.0.0", {"start": v(77.07, 9.3) * mm, "mid": v(73.7, 8.14) * mm, "end": v(71, 5.8) * mm});
            skLineSegment(sketch, "E44.4.0.1", {"start": v(71, 5.8) * mm, "end": v(138.42, -110.96) * mm});
            skLineSegment(sketch, "E44.4.0.2", {"start": v(77.07, 9.3) * mm, "end": v(144.34, -107.21) * mm});
            skArc(sketch, "E44.4.0.3", {"start": v(138.42, -110.96) * mm, "mid": v(141.74, -109.66) * mm, "end": v(144.34, -107.21) * mm});
            skArc(sketch, "E44.5.0.0", {"start": v(96.67, 9.3) * mm, "mid": v(93.3, 8.14) * mm, "end": v(90.6, 5.8) * mm});
            skLineSegment(sketch, "E44.5.0.1", {"start": v(90.6, 5.8) * mm, "end": v(158.02, -110.96) * mm});
            skLineSegment(sketch, "E44.5.0.2", {"start": v(96.67, 9.3) * mm, "end": v(163.94, -107.21) * mm});
            skArc(sketch, "E44.5.0.3", {"start": v(158.02, -110.96) * mm, "mid": v(161.34, -109.66) * mm, "end": v(163.94, -107.21) * mm});
            skArc(sketch, "E44.6.0.0", {"start": v(116.27, 9.3) * mm, "mid": v(112.9, 8.14) * mm, "end": v(110.2, 5.8) * mm});
            skLineSegment(sketch, "E44.6.0.1", {"start": v(110.2, 5.8) * mm, "end": v(177.62, -110.96) * mm});
            skLineSegment(sketch, "E44.6.0.2", {"start": v(116.27, 9.3) * mm, "end": v(183.54, -107.21) * mm});
            skArc(sketch, "E44.6.0.3", {"start": v(177.62, -110.96) * mm, "mid": v(180.94, -109.66) * mm, "end": v(183.54, -107.21) * mm});
            skArc(sketch, "E44.7.0.0", {"start": v(135.87, 9.3) * mm, "mid": v(132.5, 8.14) * mm, "end": v(129.8, 5.8) * mm});
            skLineSegment(sketch, "E44.7.0.1", {"start": v(129.8, 5.8) * mm, "end": v(197.22, -110.96) * mm});
            skLineSegment(sketch, "E44.7.0.2", {"start": v(135.87, 9.3) * mm, "end": v(203.14, -107.21) * mm});
            skArc(sketch, "E44.7.0.3", {"start": v(197.22, -110.96) * mm, "mid": v(200.54, -109.66) * mm, "end": v(203.14, -107.21) * mm});
            skArc(sketch, "E44.8.0.0", {"start": v(155.47, 9.3) * mm, "mid": v(152.1, 8.14) * mm, "end": v(149.4, 5.8) * mm});
            skLineSegment(sketch, "E44.8.0.1", {"start": v(149.4, 5.8) * mm, "end": v(216.82, -110.96) * mm});
            skLineSegment(sketch, "E44.8.0.2", {"start": v(155.47, 9.3) * mm, "end": v(222.74, -107.21) * mm});
            skArc(sketch, "E44.8.0.3", {"start": v(216.82, -110.96) * mm, "mid": v(220.14, -109.66) * mm, "end": v(222.74, -107.21) * mm});
            skArc(sketch, "E44.9.0.0", {"start": v(175.07, 9.3) * mm, "mid": v(171.7, 8.14) * mm, "end": v(169, 5.8) * mm});
            skLineSegment(sketch, "E44.9.0.1", {"start": v(169, 5.8) * mm, "end": v(236.42, -110.96) * mm});
            skLineSegment(sketch, "E44.9.0.2", {"start": v(175.07, 9.3) * mm, "end": v(242.34, -107.21) * mm});
            skArc(sketch, "E44.9.0.3", {"start": v(236.42, -110.96) * mm, "mid": v(239.74, -109.66) * mm, "end": v(242.34, -107.21) * mm});
            skArc(sketch, "E44.10.0.0", {"start": v(194.67, 9.3) * mm, "mid": v(191.3, 8.14) * mm, "end": v(188.6, 5.8) * mm});
            skLineSegment(sketch, "E44.10.0.1", {"start": v(188.6, 5.8) * mm, "end": v(256.02, -110.96) * mm});
            skLineSegment(sketch, "E44.10.0.2", {"start": v(194.67, 9.3) * mm, "end": v(261.94, -107.21) * mm});
            skArc(sketch, "E44.10.0.3", {"start": v(256.02, -110.96) * mm, "mid": v(259.34, -109.66) * mm, "end": v(261.94, -107.21) * mm});
            skArc(sketch, "E44.11.0.0", {"start": v(214.27, 9.3) * mm, "mid": v(210.9, 8.14) * mm, "end": v(208.2, 5.8) * mm});
            skLineSegment(sketch, "E44.11.0.1", {"start": v(208.2, 5.8) * mm, "end": v(275.62, -110.96) * mm});
            skLineSegment(sketch, "E44.11.0.2", {"start": v(214.27, 9.3) * mm, "end": v(281.54, -107.21) * mm});
            skArc(sketch, "E44.11.0.3", {"start": v(275.62, -110.96) * mm, "mid": v(278.94, -109.66) * mm, "end": v(281.54, -107.21) * mm});
            skArc(sketch, "E44.12.0.0", {"start": v(233.87, 9.3) * mm, "mid": v(230.5, 8.14) * mm, "end": v(227.8, 5.8) * mm});
            skLineSegment(sketch, "E44.12.0.1", {"start": v(227.8, 5.8) * mm, "end": v(295.22, -110.96) * mm});
            skLineSegment(sketch, "E44.12.0.2", {"start": v(233.87, 9.3) * mm, "end": v(301.14, -107.21) * mm});
            skArc(sketch, "E44.12.0.3", {"start": v(295.22, -110.96) * mm, "mid": v(298.54, -109.66) * mm, "end": v(301.14, -107.21) * mm});
            skArc(sketch, "E44.13.0.0", {"start": v(253.47, 9.3) * mm, "mid": v(250.1, 8.14) * mm, "end": v(247.4, 5.8) * mm});
            skLineSegment(sketch, "E44.13.0.1", {"start": v(247.4, 5.8) * mm, "end": v(314.82, -110.96) * mm});
            skLineSegment(sketch, "E44.13.0.2", {"start": v(253.47, 9.3) * mm, "end": v(320.74, -107.21) * mm});
            skArc(sketch, "E44.13.0.3", {"start": v(314.82, -110.96) * mm, "mid": v(318.14, -109.66) * mm, "end": v(320.74, -107.21) * mm});
            skArc(sketch, "E44.14.0.0", {"start": v(273.07, 9.3) * mm, "mid": v(269.7, 8.14) * mm, "end": v(267, 5.8) * mm});
            skLineSegment(sketch, "E44.14.0.1", {"start": v(267, 5.8) * mm, "end": v(334.42, -110.96) * mm});
            skLineSegment(sketch, "E44.14.0.2", {"start": v(273.07, 9.3) * mm, "end": v(340.34, -107.21) * mm});
            skArc(sketch, "E44.14.0.3", {"start": v(334.42, -110.96) * mm, "mid": v(337.74, -109.66) * mm, "end": v(340.34, -107.21) * mm});
            skArc(sketch, "E44.15.0.0", {"start": v(292.67, 9.3) * mm, "mid": v(289.3, 8.14) * mm, "end": v(286.6, 5.8) * mm});
            skLineSegment(sketch, "E44.15.0.1", {"start": v(286.6, 5.8) * mm, "end": v(354.02, -110.96) * mm});
            skLineSegment(sketch, "E44.15.0.2", {"start": v(292.67, 9.3) * mm, "end": v(359.94, -107.21) * mm});
            skArc(sketch, "E44.15.0.3", {"start": v(354.02, -110.96) * mm, "mid": v(357.34, -109.66) * mm, "end": v(359.94, -107.21) * mm});
            skArc(sketch, "E44.16.0.0", {"start": v(312.27, 9.3) * mm, "mid": v(308.9, 8.14) * mm, "end": v(306.2, 5.8) * mm});
            skLineSegment(sketch, "E44.16.0.1", {"start": v(306.2, 5.8) * mm, "end": v(373.62, -110.96) * mm});
            skLineSegment(sketch, "E44.16.0.2", {"start": v(312.27, 9.3) * mm, "end": v(379.54, -107.21) * mm});
            skArc(sketch, "E44.16.0.3", {"start": v(373.62, -110.96) * mm, "mid": v(376.94, -109.66) * mm, "end": v(379.54, -107.21) * mm});
            skArc(sketch, "E44.17.0.0", {"start": v(331.87, 9.3) * mm, "mid": v(328.5, 8.14) * mm, "end": v(325.8, 5.8) * mm});
            skLineSegment(sketch, "E44.17.0.1", {"start": v(325.8, 5.8) * mm, "end": v(393.22, -110.96) * mm});
            skLineSegment(sketch, "E44.17.0.2", {"start": v(331.87, 9.3) * mm, "end": v(399.14, -107.21) * mm});
            skArc(sketch, "E44.17.0.3", {"start": v(393.22, -110.96) * mm, "mid": v(396.54, -109.66) * mm, "end": v(399.14, -107.21) * mm});
            skArc(sketch, "E44.18.0.0", {"start": v(351.47, 9.3) * mm, "mid": v(348.1, 8.14) * mm, "end": v(345.4, 5.8) * mm});
            skLineSegment(sketch, "E44.18.0.1", {"start": v(345.4, 5.8) * mm, "end": v(412.82, -110.96) * mm});
            skLineSegment(sketch, "E44.18.0.2", {"start": v(351.47, 9.3) * mm, "end": v(418.74, -107.21) * mm});
            skArc(sketch, "E44.18.0.3", {"start": v(412.82, -110.96) * mm, "mid": v(416.14, -109.66) * mm, "end": v(418.74, -107.21) * mm});
            skArc(sketch, "E44.19.0.0", {"start": v(371.07, 9.3) * mm, "mid": v(367.7, 8.14) * mm, "end": v(365, 5.8) * mm});
            skLineSegment(sketch, "E44.19.0.1", {"start": v(365, 5.8) * mm, "end": v(432.42, -110.96) * mm});
            skLineSegment(sketch, "E44.19.0.2", {"start": v(371.07, 9.3) * mm, "end": v(438.34, -107.21) * mm});
            skArc(sketch, "E44.19.0.3", {"start": v(432.42, -110.96) * mm, "mid": v(435.74, -109.66) * mm, "end": v(438.34, -107.21) * mm});
            skLineSegment(sketch, "E44.direction1", {"start": v(-7.4, 5.8) * mm, "end": v(12.2, 5.8) * mm, "construction": true});
            skSolve(sketch);
        }
        {
            var Q0;
            Q0 = qSketchRegion(id + "F6", true);
            extrude(context, id + "F7", {"entities" : qUnion([Q0]), "operationType" : NewBodyOperationType.REMOVE, "oppositeDirection" : true, "depth" : 2 * mm});
        }
    });
